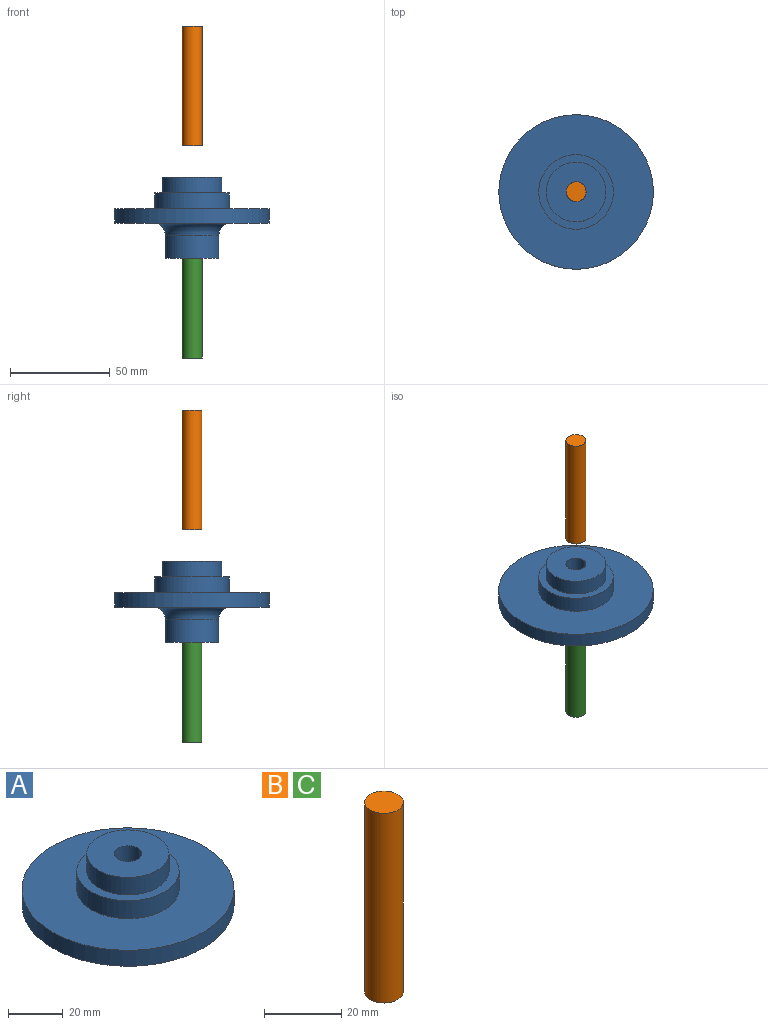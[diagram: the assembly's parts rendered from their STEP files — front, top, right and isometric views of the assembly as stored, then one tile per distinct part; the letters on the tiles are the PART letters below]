
ASSEMBLY  parts=3 mates=2
PART A: 11 faces, bbox 77.4x77.4x40.5 mm
  f0: plane 26.96x26.96mm, normal (0,0,-1), area 492.4mm2, adj f1,f10
  f1: cylinder r=13.48mm len=26.96mm, axis (0,0,-1), area 979.6mm2, adj f0,f2
  f2: torus R=19.48mm, axis (0,0,-1), area 927.4mm2, adj f1,f3
  f3: plane 77.39x77.39mm, normal (0,0,-1), area 3511.1mm2, adj f2,f4
  f4: cylinder r=38.69mm len=77.39mm, axis (0,0,-1), area 1726.1mm2, adj f3,f5
  f5: plane 77.39x77.39mm, normal (0,0,1), area 3605.6mm2, adj f4,f6
  f6: cylinder r=18.69mm len=37.39mm, axis (0,0,-1), area 939.6mm2, adj f5,f7
  f7: plane 37.39x37.39mm, normal (0,0,1), area 390.9mm2, adj f6,f8
  f8: cylinder r=15mm len=30mm, axis (0,0,-1), area 737.6mm2, adj f7,f9
  f9: plane 30x30mm, normal (0,0,1), area 628.3mm2, adj f8,f10
  f10: cylinder r=5mm len=40.49mm, axis (0,0,-1), area 1272.1mm2, adj f0,f9
PART B: 3 faces, bbox 10x10x60 mm
  f0: cylinder r=5mm len=60mm, axis (0,0,-1), area 1885mm2, adj f1,f2
  f1: plane 10x10mm, normal (0,0,1), area 78.5mm2, adj f0
  f2: plane 10x10mm, normal (0,0,-1), area 78.5mm2, adj f0
PART C: same geometry as B
PLACE A t=(6.51,3.32,0)mm fixed
PLACE B t=(6.51,3.32,56.27)mm
PLACE C rot(axis=(0,0,-1),177.1deg) t=(6.51,3.32,-50.06)mm
MATE cylindrical C.f0 <-> A.f1  axis (0,0,-1) through (6.51,3.32,-20.06)mm
MATE slider B.f0 <-> A.f1  axis (0,0,-1) through (6.51,3.32,86.27)mm
